# Revit family: Crealco Skyline Heavy Duty Sash Top Hung D
name_source: partatom
category: Windows
revit_build: Autodesk Revit 2014 (Build: 20130308_1515(x64)
units: mm (PartAtom-declared; Revit-internal decimal feet)

## types (12) — shared parameters
Corrected Mullion Configuration = 2 mm  [stored 0.00656168 ft]
Custom Sash Height = 502 mm
Description = Top Hung Type D Standard Sash Window
Frame Profile Thickness = 41 mm  [stored 0.134514 ft]
Heavy Duty Sash = Yes
Limit Fixed Pane Height Max = 3000 mm  [stored 9.84252 ft]
Limit Fixed Pane Height Min = 200 mm  [stored 0.656168 ft]
Limit Fixed Pane Width Max = 3000 mm  [stored 9.84252 ft]
Limit Fixed Pane Width Min = 200 mm  [stored 0.656168 ft]
Limit Sash Height Max = 1200 mm  [stored 3.93701 ft]
Limit Sash Height Min = 300 mm  [stored 0.984252 ft]
Limit Sash Width Max = 1500 mm  [stored 4.92126 ft]
Limit Sash Width Min = 300 mm  [stored 0.984252 ft]
Limit Window Width Min = 388 mm
Manufacturer = Crealco
Max System DG Unit Thickness = 25 mm  [stored 0.082021 ft]
Model = Skyline
Rough Width = 3 mm  [stored 0.00984252 ft]
Sash Side Gap = 44 mm
Standard Mullion Different = No
Standard Sash = No
URL = www.crealco.co.za
Wall Closure = By host
zero-valued in all types: Custom Frame Offset From Exterior

## per-type parameters (varying)
| type | Clearvue Insulated LowE SHGC Value | Clearvue Insulated LowE U Value | Clearvue Insulated SHGC Value | Clearvue Insulated U Value | Clearvue SHGC Value | Clearvue U Value | Custom Windload | Custom Window Height | Custom Window Width | Energy Advantage SHGC Value | Energy Advantage U Value | Intruderprufe Insulated LowE SHGC Value | Intruderprufe Insulated LowE U Value | Intruderprufe Insulated SHGC Value | Intruderprufe Insulated U Value | Intruderprufe LowE SHGC Value | Intruderprufe LowE U Value | Intruderprufe SHGC Value | Intruderprufe U Value | Toughened Safety SHGC Value | Toughened Safety U Value |
| 0600 x 0900mm 1000Pa | 0.736 | 3.8 | 0.736 | 3.89 | 0.427 | 6.2 | 1000 mm  [stored 3.28084 ft] | 890 mm  [stored 2.91995 ft] | 590 mm  [stored 1.9357 ft] | 0.387 | 5.43 | 0.611 | 2.78 | 0.611 | 2.84 | 0.36 | 5.26 | 0.403 | 6.05 | 0.427 | 6.2 |
| 0600 x 0900mm 1500Pa | 0.736 | 3.8 | 0.736 | 3.89 | 0.427 | 6.2 | 1500 mm  [stored 4.92126 ft] | 890 mm  [stored 2.91995 ft] | 590 mm  [stored 1.9357 ft] | 0.387 | 5.43 | 0.611 | 2.78 | 0.611 | 2.84 | 0.36 | 5.26 | 0.403 | 6.05 | 0.427 | 6.2 |
| 0600 x 0900mm 2000Pa | 0.736 | 3.8 | 0.736 | 3.89 | 0.427 | 6.2 | 2000 mm  [stored 6.56168 ft] | 890 mm  [stored 2.91995 ft] | 590 mm  [stored 1.9357 ft] | 0.387 | 5.43 | 0.611 | 2.78 | 0.611 | 2.84 | 0.36 | 5.26 | 0.403 | 6.05 | 0.427 | 6.2 |
| 0600 x 1200mm 1000Pa | 0.764 | 4.01 | 0.764 | 4.07 | 0.494 | 6.15 | 1000 mm  [stored 3.28084 ft] | 1190 mm  [stored 3.9042 ft] | 590 mm  [stored 1.9357 ft] | 0.445 | 5.16 | 0.635 | 2.8 | 0.635 | 2.84 | 0.414 | 4.98 | 0.465 | 5.97 | 0.494 | 6.15 |
| 0600 x 1200mm 1500Pa | 0.764 | 4.01 | 0.764 | 4.07 | 0.494 | 6.15 | 1500 mm  [stored 4.92126 ft] | 1190 mm  [stored 3.9042 ft] | 590 mm  [stored 1.9357 ft] | 0.445 | 5.16 | 0.635 | 2.8 | 0.635 | 2.84 | 0.414 | 4.98 | 0.465 | 5.97 | 0.494 | 6.15 |
| 0600 x 1200mm 2000Pa | 0.764 | 4.01 | 0.764 | 4.07 | 0.494 | 6.15 | 2000 mm  [stored 6.56168 ft] | 1190 mm  [stored 3.9042 ft] | 590 mm  [stored 1.9357 ft] | 0.445 | 5.16 | 0.635 | 2.8 | 0.635 | 2.84 | 0.414 | 4.98 | 0.465 | 5.97 | 0.494 | 6.15 |
| 0900 x 0900mm 1000Pa | 0.736 | 4.1 | 0.736 | 4.18 | 0.482 | 6.16 | 1000 mm  [stored 3.28084 ft] | 890 mm  [stored 2.91995 ft] | 890 mm  [stored 2.91995 ft] | 0.435 | 5.21 | 0.611 | 2.98 | 0.611 | 3.04 | 0.405 | 5.06 | 0.454 | 6.02 | 0.482 | 6.16 |
| 0900 x 0900mm 1500Pa | 0.736 | 4.1 | 0.736 | 4.18 | 0.482 | 6.16 | 1500 mm  [stored 4.92126 ft] | 890 mm  [stored 2.91995 ft] | 890 mm  [stored 2.91995 ft] | 0.435 | 5.21 | 0.611 | 2.98 | 0.611 | 3.04 | 0.405 | 5.06 | 0.454 | 6.02 | 0.482 | 6.16 |
| 0900 x 0900mm 2000Pa | 0.736 | 4.1 | 0.736 | 4.18 | 0.482 | 6.16 | 2000 mm  [stored 6.56168 ft] | 890 mm  [stored 2.91995 ft] | 890 mm  [stored 2.91995 ft] | 0.435 | 5.21 | 0.611 | 2.98 | 0.611 | 3.04 | 0.405 | 5.06 | 0.454 | 6.02 | 0.482 | 6.16 |
| 0900 x 1200mm 1000Pa | 0.765 | 4.33 | 0.765 | 4.4 | 0.548 | 6.11 | 1000 mm  [stored 3.28084 ft] | 1190 mm  [stored 3.9042 ft] | 890 mm  [stored 2.91995 ft] | 0.493 | 4.94 | 0.635 | 3.01 | 0.635 | 3.06 | 0.459 | 4.79 | 0.516 | 5.95 | 0.548 | 6.11 |
| 0900 x 1200mm 1500Pa | 0.765 | 4.33 | 0.765 | 4.4 | 0.548 | 6.11 | 1500 mm  [stored 4.92126 ft] | 1190 mm  [stored 3.9042 ft] | 890 mm  [stored 2.91995 ft] | 0.493 | 4.94 | 0.635 | 3.01 | 0.635 | 3.06 | 0.459 | 4.79 | 0.516 | 5.95 | 0.548 | 6.11 |
| 0900 x 1200mm 2000Pa | 0.765 | 4.33 | 0.765 | 4.4 | 0.548 | 6.11 | 2000 mm  [stored 6.56168 ft] | 1190 mm  [stored 3.9042 ft] | 890 mm  [stored 2.91995 ft] | 0.493 | 4.94 | 0.635 | 3.01 | 0.635 | 3.06 | 0.459 | 4.79 | 0.516 | 5.95 | 0.548 | 6.11 |

note: [stored X ft] marks values corroborated as IEEE doubles in the binary element streams (Revit-internal decimal feet)

## geometry (parser evidence)
native form markers: Sweep x18
no freeform markers — native parametric forms only
